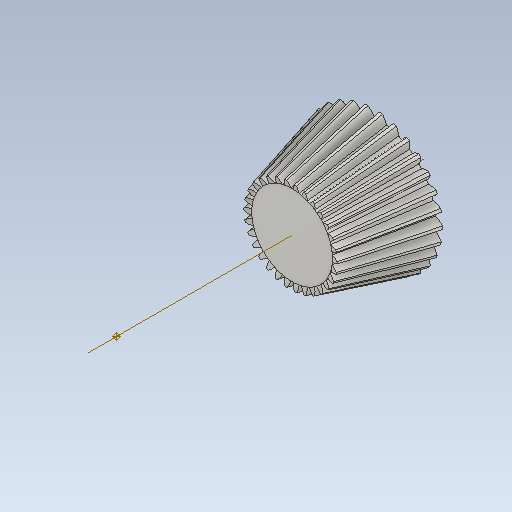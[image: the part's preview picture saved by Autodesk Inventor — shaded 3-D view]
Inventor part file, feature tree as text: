
AUTODESK INVENTOR PART (.ipt)
format: ipt  version: 2021 (Build 250183000, 183)  size: 672,768 bytes
history: native  units: mm
features: other x24, loft x2, pattern_circular x2, sketch x1
ambient origin geometry x6: Origin, XZ Plane, X Axis, Y Axis, Z Axis, Center Point
bodies: Solid1 (feature_tree)
feature tree (29):
  other  "Top Point"
  other  "Mesh Plane2"
  other  "Teeth Body"
  other  "Start Point"
  other  "Tooth Plane"
  other  "Start Sketch"
  other  "End Point"
  other  "3D Sketch Right"
  other  "End Plane Right"
  loft  "Loft Right"
  pattern_circular  "Circular Pattern Right"  [2 undecoded]
  other  "3D Sketch Left"
  other  "End Plane Left"
  loft  "Loft Left"
  pattern_circular  "Circular Pattern Left"  [2 undecoded]
  other  "Fix Body"
  other  "Mesh Plane"
  other  "Top Plane"
  other  "Teeth Body Sketch"
  other  "End Plane"
  other  "End Sketch"
  other  "Helical Curve Left"
  other  "End Sketch Left"
  other  "Body Sketch"
  sketch  "Sketch6"  dims[d0=38.1mm d1=35.143006mm d2=40.564162mm d3=25.4mm d4=75.89198mm d5=90.0deg d7=7.149344mm d8=7.57366mm d9=16.807212mm d11=25.5397mm d12=4.824667mm d15=5.111013mm d16=11.342189mm d17=0.0mm d18=90.0deg d19=0.0mm d20=90.0deg d21=300.0mm d22=360.0deg d26=267.453903mm d27=24.777148mm d28=38.1mm d29=-2.449787mm d30=4.824667mm d31=5.111013mm d32=11.342189mm d35=0.0mm d37=0.0mm d39=0.0mm d40=90.0deg d41=300.0mm d42=360.0deg d46=90.0deg d47=90.0deg d48=0.0mm d49=0.0mm d50=90.0deg d51=1.047198mm d52=0.0mm d53=0.0mm d54=0.0mm d56=13.314988mm d57=21.744491mm d58=17.777011mm d59=14.674064mm d60=11.996648mm d61=14.674064mm d62=11.996648mm d63=90.0deg d64=90.0deg d65=267.453903mm d66=31.5mm d67=38.1mm d68=-2.449787mm d69=24.777148mm d70=5.111013mm d71=11.342189mm d72=4.824667mm d73=11.996648mm d74=14.674064mm d75=0.0mm d76=90.0deg d77=0.0mm d78=90.0deg d79=0.0mm d80=90.0deg d81=300.0mm d82=360.0deg d84=10.0mm d85=20.0mm d86=20.0mm d87=10.0mm d88=0.0mm d89=0.0mm]
  other  "Srf1"
  other  "Helical Curve Right"
  other  "End Sketch Right"
  other  "Pitch Diameter"
note: 4 required parameter values undecoded (feature->parameter linkage not recoverable at this tier; creation-order binding heuristic only, values carry confidence <= 0.55)
